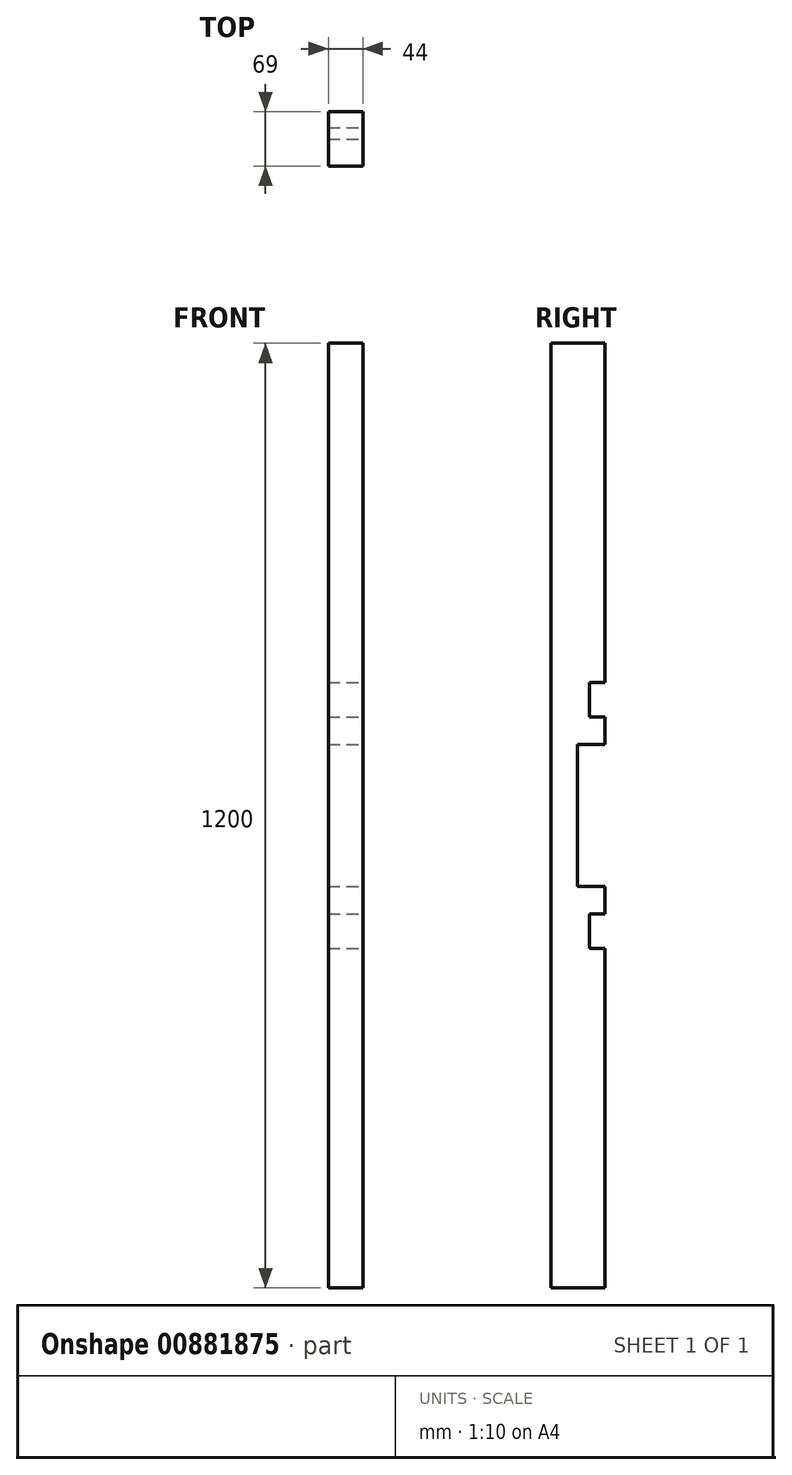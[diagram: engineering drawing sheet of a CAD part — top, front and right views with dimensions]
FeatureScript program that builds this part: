
annotation { "Feature Type Name" : "Feature", "Feature Type Description" : "" }
export const myFeature = defineFeature(function(context is Context, id is Id, definition is map)
    precondition{}
    {
        {
            var Q0;
            Q0=qCreatedBy(makeId("Top.planeOp"),FACE);
            var sketch = newSketch(context, id + "F0", { "sketchPlane" : qUnion([Q0])});
            skLineSegment(sketch, "E0.bottom", {"start": v(22, -34.5) * mm, "end": v(-22, -34.5) * mm});
            skLineSegment(sketch, "E0.top", {"start": v(22, 34.5) * mm, "end": v(-22, 34.5) * mm});
            skLineSegment(sketch, "E0.left", {"start": v(22, -34.5) * mm, "end": v(22, 34.5) * mm});
            skLineSegment(sketch, "E0.right", {"start": v(-22, -34.5) * mm, "end": v(-22, 34.5) * mm});
            skPoint(sketch, "E0.middle", {"position": v(0, 0) * mm});
            skSolve(sketch);
        }
        {
            var Q0;
            Q0=qSketchRegion(id+"F0",true);
            extrude(context, id + "F1", {"entities" : qUnion([Q0]), "depth" : 1200 * mm, "offsetDistance" : 25 * mm});
        }
        {
            var Q0;
            Q0=makeQuery(id+"F1.opExtrude","SWEPT_FACE",FACE,{"disambiguationData":[OSD([sQuery(id+"F0.wireOp",EDGE,"E0.left")])]});
            var sketch = newSketch(context, id + "F2", { "sketchPlane" : qUnion([Q0])});
            skLineSegment(sketch, "E1", {"start": v(34.5, 600) * mm, "end": v(-34.5, 600) * mm, "construction": true});
            skLineSegment(sketch, "E2", {"start": v(34.5, 510) * mm, "end": v(-0.5, 510) * mm});
            skLineSegment(sketch, "E3", {"start": v(-0.5, 510) * mm, "end": v(-0.5, 600) * mm});
            skLineSegment(sketch, "E4.MirrorCS", {"start": v(-0.5, 690) * mm, "end": v(-0.5, 600) * mm});
            skLineSegment(sketch, "E5.MirrorCS", {"start": v(34.5, 690) * mm, "end": v(-0.5, 690) * mm});
            skLineSegment(sketch, "E6", {"start": v(34.5, 510) * mm, "end": v(34.5, 600) * mm});
            skLineSegment(sketch, "E7.MirrorCS", {"start": v(34.5, 690) * mm, "end": v(34.5, 600) * mm});
            skLineSegment(sketch, "E8", {"start": v(34.5, 475) * mm, "end": v(14.5, 475) * mm});
            skLineSegment(sketch, "E9", {"start": v(14.5, 475) * mm, "end": v(14.5, 431) * mm});
            skLineSegment(sketch, "E10", {"start": v(14.5, 431) * mm, "end": v(34.5, 431) * mm});
            skLineSegment(sketch, "E11", {"start": v(34.5, 475) * mm, "end": v(34.5, 431) * mm});
            skLineSegment(sketch, "E12.MirrorCS", {"start": v(14.5, 769) * mm, "end": v(34.5, 769) * mm});
            skLineSegment(sketch, "E13.MirrorCS", {"start": v(34.5, 725) * mm, "end": v(34.5, 769) * mm});
            skLineSegment(sketch, "E14.MirrorCS", {"start": v(34.5, 725) * mm, "end": v(14.5, 725) * mm});
            skLineSegment(sketch, "E15.MirrorCS", {"start": v(14.5, 725) * mm, "end": v(14.5, 769) * mm});
            skSolve(sketch);
        }
        {
            var Q0;
            Q0=qSketchRegion(id+"F2",true);
            extrude(context, id + "F3", {"entities" : qUnion([Q0]), "operationType" : NewBodyOperationType.REMOVE, "endBound" : BoundingType.THROUGH_ALL, "oppositeDirection" : true, "depth" : 25 * mm, "offsetDistance" : 25 * mm});
        }
    });
